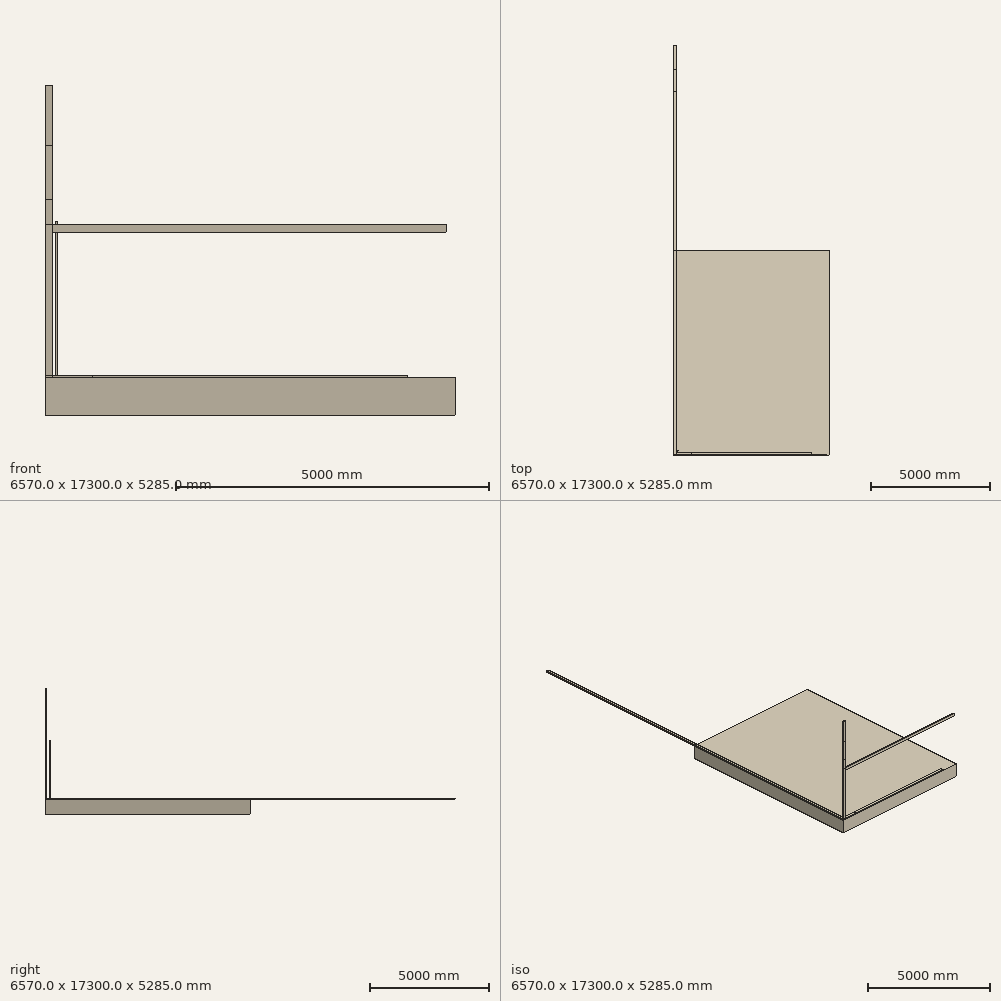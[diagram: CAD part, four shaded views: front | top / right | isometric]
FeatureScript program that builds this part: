
annotation { "Feature Type Name" : "Feature", "Feature Type Description" : "" }
export const myFeature = defineFeature(function(context is Context, id is Id, definition is map)
    precondition{}
    {
        {
            var Q0;
            Q0=qCreatedBy(makeId("Top.planeOp"),FACE);
            var sketch = newSketch(context, id + "F0", { "sketchPlane" : qUnion([Q0])});
            skLineSegment(sketch, "E0.bottom", {"start": v(0, 0) * mm, "end": v(6570, 0) * mm});
            skLineSegment(sketch, "E0.top", {"start": v(0, 8670) * mm, "end": v(6570, 8670) * mm});
            skLineSegment(sketch, "E0.left", {"start": v(0, 0) * mm, "end": v(0, 8670) * mm});
            skLineSegment(sketch, "E0.right", {"start": v(6570, 0) * mm, "end": v(6570, 8670) * mm});
            skSolve(sketch);
        }
        {
            var Q0;
            Q0=makeQuery(id+"F0.imprint","IMPRINT",FACE,{"disambiguationData":[TD([[makeQuery(id+"F0.imprint","IMPRINT",EDGE,{"derivedFrom":sQuery(id+"F0.wireOp",EDGE,"E0.bottom")}),1.0]])]});
            extrude(context, id + "F1", {"entities" : qUnion([Q0]), "oppositeDirection" : true, "depth" : 600 * mm, "offsetDistance" : 25 * mm});
        }
        {
            var Q0;
            Q0=makeQuery(id+"F1.opExtrude","SWEPT_FACE",FACE,{"disambiguationData":[OSD([sQuery(id+"F0.wireOp",EDGE,"E0.bottom")])]});
            var sketch = newSketch(context, id + "F2", { "sketchPlane" : qUnion([Q0])});
            skLineSegment(sketch, "E1.bottom", {"start": v(0, 0) * mm, "end": v(120, 0) * mm});
            skLineSegment(sketch, "E1.top", {"start": v(0, 45) * mm, "end": v(120, 45) * mm});
            skLineSegment(sketch, "E1.left", {"start": v(0, 0) * mm, "end": v(0, 45) * mm});
            skLineSegment(sketch, "E1.right", {"start": v(120, 0) * mm, "end": v(120, 45) * mm});
            skSolve(sketch);
        }
        {
            var Q0;
            Q0=makeQuery(id+"F2.imprint","IMPRINT",FACE,{"disambiguationData":[TD([[makeQuery(id+"F2.imprint","IMPRINT",EDGE,{"derivedFrom":sQuery(id+"F2.wireOp",EDGE,"E1.bottom")}),1.0]])]});
            extrude(context, id + "F3", {"entities" : qUnion([Q0]), "oppositeDirection" : true, "depth" : 8650 * mm, "offsetDistance" : 25 * mm});
        }
        {
            var Q0;
            Q0=makeQuery(id+"F3.opExtrude","SWEPT_FACE",FACE,{"disambiguationData":[OSD([sQuery(id+"F2.wireOp",EDGE,"E1.top")])]});
            var sketch = newSketch(context, id + "F4", { "sketchPlane" : qUnion([Q0])});
            skLineSegment(sketch, "E2.bottom", {"start": v(0, 0) * mm, "end": v(120, 0) * mm});
            skLineSegment(sketch, "E2.top", {"start": v(0, 45) * mm, "end": v(120, 45) * mm});
            skLineSegment(sketch, "E2.left", {"start": v(0, 0) * mm, "end": v(0, 45) * mm});
            skLineSegment(sketch, "E2.right", {"start": v(120, 0) * mm, "end": v(120, 45) * mm});
            skSolve(sketch);
        }
        {
            var Q0;
            Q0=makeQuery(id+"F4.imprint","IMPRINT",FACE,{"disambiguationData":[TD([[makeQuery(id+"F4.imprint","IMPRINT",EDGE,{"derivedFrom":sQuery(id+"F4.wireOp",EDGE,"E2.bottom")}),1.0]])]});
            extrude(context, id + "F5", {"entities" : qUnion([Q0]), "depth" : 2410 * mm, "offsetDistance" : 25 * mm});
        }
        {
            var Q0;
            Q0=makeQuery(id+"F3.opExtrude","SWEPT_FACE",FACE,{"disambiguationData":[OSD([sQuery(id+"F2.wireOp",EDGE,"E1.right")])]});
            var sketch = newSketch(context, id + "F6", { "sketchPlane" : qUnion([Q0])});
            skLineSegment(sketch, "E3.bottom", {"start": v(0, 0) * mm, "end": v(120, 0) * mm});
            skLineSegment(sketch, "E3.top", {"start": v(0, 45) * mm, "end": v(120, 45) * mm});
            skLineSegment(sketch, "E3.left", {"start": v(0, 0) * mm, "end": v(0, 45) * mm});
            skLineSegment(sketch, "E3.right", {"start": v(120, 0) * mm, "end": v(120, 45) * mm});
            skSolve(sketch);
        }
        {
            var Q0;
            Q0 = qSketchRegion(id + "F6", true);
            extrude(context, id + "F7", {"entities" : qUnion([Q0]), "depth" : 638 * mm, "offsetDistance" : 25 * mm});
        }
        {
            var Q0;
            Q0=makeQuery(id+"F5.opExtrude","SWEPT_FACE",FACE,{"disambiguationData":[OSD([sQuery(id+"F4.wireOp",EDGE,"E2.right")])]});
            var sketch = newSketch(context, id + "F8", { "sketchPlane" : qUnion([Q0])});
            skLineSegment(sketch, "E4.bottom", {"start": v(0, 2455) * mm, "end": v(45, 2455) * mm});
            skLineSegment(sketch, "E4.top", {"start": v(0, 2335) * mm, "end": v(45, 2335) * mm});
            skLineSegment(sketch, "E4.left", {"start": v(0, 2455) * mm, "end": v(0, 2335) * mm});
            skLineSegment(sketch, "E4.right", {"start": v(45, 2455) * mm, "end": v(45, 2335) * mm});
            skSolve(sketch);
        }
        {
            var Q0;
            Q0=makeQuery(id+"F8.imprint","IMPRINT",FACE,{"disambiguationData":[TD([[makeQuery(id+"F8.imprint","IMPRINT",EDGE,{"derivedFrom":sQuery(id+"F8.wireOp",EDGE,"E4.bottom")}),1.0]])]});
            extrude(context, id + "F9", {"entities" : qUnion([Q0]), "depth" : 6310 * mm, "offsetDistance" : 25 * mm});
        }
        {
            var Q0;
            Q0=makeQuery(id+"F7.opExtrude","CAP_FACE",FACE,{"disambiguationData":[OSD([sQuery(id+"F6.wireOp",EDGE,"E3.bottom"),sQuery(id+"F6.wireOp",EDGE,"E3.top"),sQuery(id+"F6.wireOp",EDGE,"E3.left"),sQuery(id+"F6.wireOp",EDGE,"E3.right")])],"isStart":false});
            extrude(context, id + "F10", {"entities" : qUnion([Q0]), "depth" : 5044 * mm, "offsetDistance" : 25 * mm});
        }
        {
            var Q0;
            Q0=makeQuery(id+"F1.opExtrude","CAP_FACE",FACE,{"disambiguationData":[OSD([sQuery(id+"F0.wireOp",EDGE,"E0.bottom"),sQuery(id+"F0.wireOp",EDGE,"E0.top"),sQuery(id+"F0.wireOp",EDGE,"E0.left"),sQuery(id+"F0.wireOp",EDGE,"E0.right")])],"isStart":true});
            var sketch = newSketch(context, id + "F11", { "sketchPlane" : qUnion([Q0])});
            skLineSegment(sketch, "E5.bottom", {"start": v(152.4, 159.83) * mm, "end": v(197.4, 159.83) * mm});
            skLineSegment(sketch, "E5.top", {"start": v(152.4, 204.83) * mm, "end": v(197.4, 204.83) * mm});
            skLineSegment(sketch, "E5.left", {"start": v(152.4, 159.83) * mm, "end": v(152.4, 204.83) * mm});
            skLineSegment(sketch, "E5.right", {"start": v(197.4, 159.83) * mm, "end": v(197.4, 204.83) * mm});
            skSolve(sketch);
        }
        {
            var Q0;
            Q0=makeQuery(id+"F11.imprint","IMPRINT",FACE,{"disambiguationData":[TD([[makeQuery(id+"F11.imprint","IMPRINT",EDGE,{"derivedFrom":sQuery(id+"F11.wireOp",EDGE,"E5.bottom")}),1.0]])]});
            extrude(context, id + "F12", {"entities" : qUnion([Q0]), "depth" : 2500 * mm, "offsetDistance" : 25 * mm});
        }
        {
            var Q0;
            Q0=makeQuery(id+"F3.opExtrude","CAP_FACE",FACE,{"disambiguationData":[OSD([sQuery(id+"F2.wireOp",EDGE,"E1.bottom"),sQuery(id+"F2.wireOp",EDGE,"E1.top"),sQuery(id+"F2.wireOp",EDGE,"E1.left"),sQuery(id+"F2.wireOp",EDGE,"E1.right")])],"isStart":false});
            extrude(context, id + "F13", {"entities" : qUnion([Q0]), "depth" : 6705 * mm, "offsetDistance" : 25 * mm});
        }
        {
            var Q0;
            Q0=makeQuery(id+"F13.opExtrude","CAP_FACE",FACE,{"disambiguationData":[OSD([sQuery(id+"F2.wireOp",EDGE,"E1.bottom"),sQuery(id+"F2.wireOp",EDGE,"E1.top"),sQuery(id+"F2.wireOp",EDGE,"E1.left"),sQuery(id+"F2.wireOp",EDGE,"E1.right")])],"isStart":false});
            extrude(context, id + "F14", {"entities" : qUnion([Q0]), "depth" : 945 * mm, "offsetDistance" : 25 * mm});
        }
        {
            var Q0;
            Q0=makeQuery(id+"F14.opExtrude","CAP_FACE",FACE,{"disambiguationData":[OSD([sQuery(id+"F2.wireOp",EDGE,"E1.bottom"),sQuery(id+"F2.wireOp",EDGE,"E1.top"),sQuery(id+"F2.wireOp",EDGE,"E1.left"),sQuery(id+"F2.wireOp",EDGE,"E1.right")])],"isStart":false});
            extrude(context, id + "F15", {"entities" : qUnion([Q0]), "depth" : 1000 * mm, "offsetDistance" : 25 * mm});
        }
        {
            var Q0;
            Q0=makeQuery(id+"F5.opExtrude","CAP_FACE",FACE,{"disambiguationData":[OSD([sQuery(id+"F4.wireOp",EDGE,"E2.bottom"),sQuery(id+"F4.wireOp",EDGE,"E2.top"),sQuery(id+"F4.wireOp",EDGE,"E2.left"),sQuery(id+"F4.wireOp",EDGE,"E2.right")])],"isStart":false});
            extrude(context, id + "F16", {"entities" : qUnion([Q0]), "depth" : 410 * mm, "offsetDistance" : 25 * mm});
        }
        {
            var Q0;
            Q0=makeQuery(id+"F16.opExtrude","CAP_FACE",FACE,{"disambiguationData":[OSD([sQuery(id+"F4.wireOp",EDGE,"E2.bottom"),sQuery(id+"F4.wireOp",EDGE,"E2.top"),sQuery(id+"F4.wireOp",EDGE,"E2.left"),sQuery(id+"F4.wireOp",EDGE,"E2.right")])],"isStart":false});
            extrude(context, id + "F17", {"entities" : qUnion([Q0]), "depth" : 865 * mm, "offsetDistance" : 25 * mm});
        }
        {
            var Q0;
            Q0=makeQuery(id+"F17.opExtrude","CAP_FACE",FACE,{"disambiguationData":[OSD([sQuery(id+"F4.wireOp",EDGE,"E2.bottom"),sQuery(id+"F4.wireOp",EDGE,"E2.top"),sQuery(id+"F4.wireOp",EDGE,"E2.left"),sQuery(id+"F4.wireOp",EDGE,"E2.right")])],"isStart":false});
            extrude(context, id + "F18", {"entities" : qUnion([Q0]), "depth" : 955 * mm, "offsetDistance" : 25 * mm});
        }
    });
